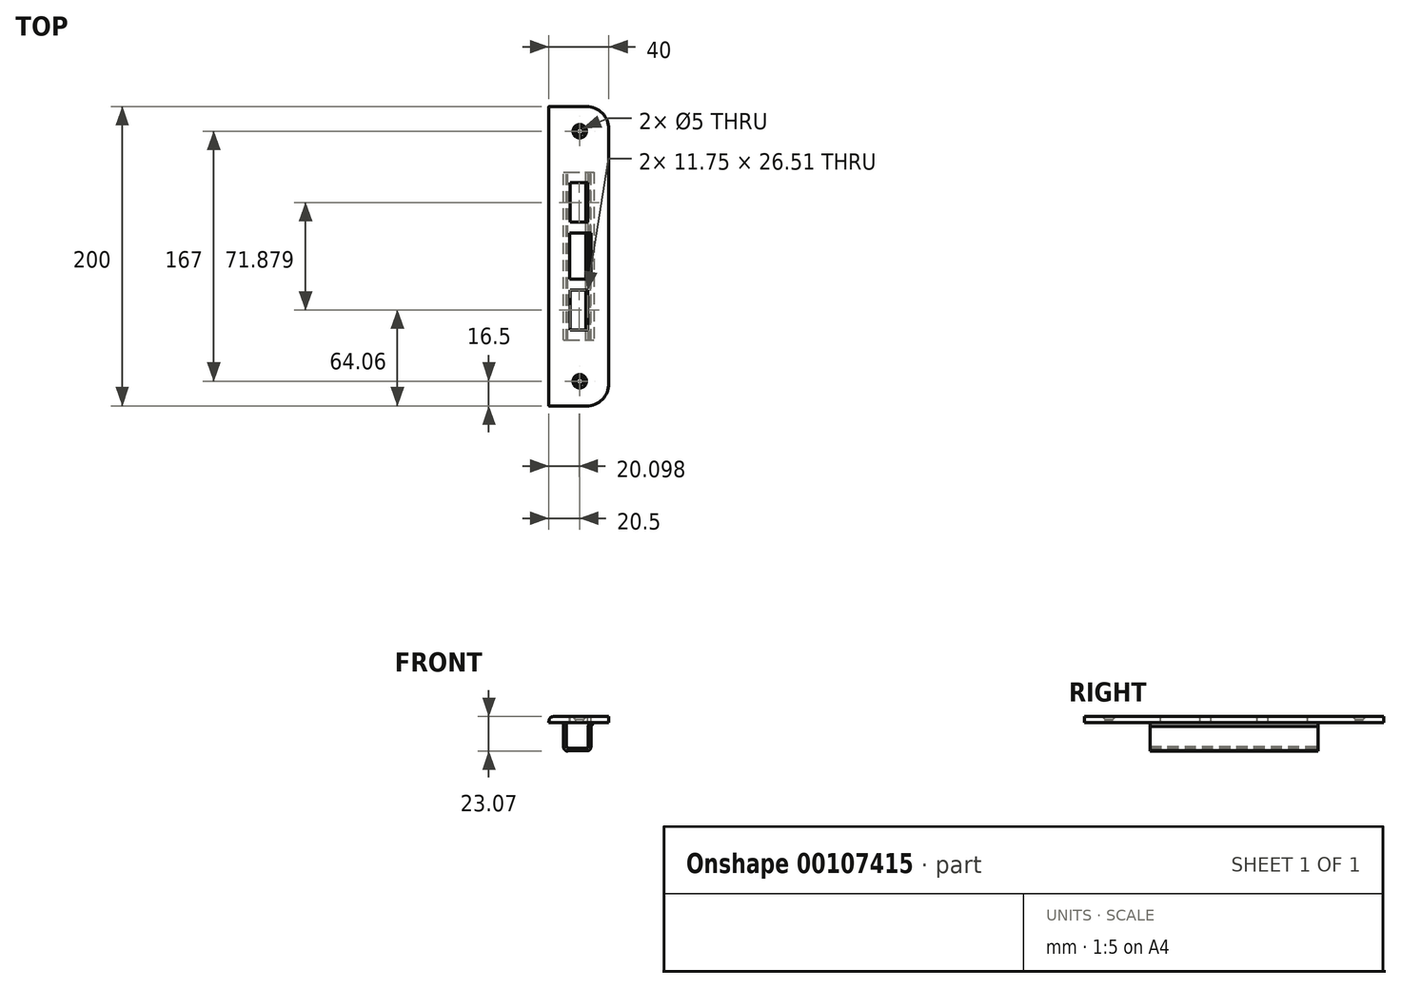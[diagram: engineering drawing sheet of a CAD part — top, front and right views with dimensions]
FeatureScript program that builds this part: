
annotation { "Feature Type Name" : "Feature", "Feature Type Description" : "" }
export const myFeature = defineFeature(function(context is Context, id is Id, definition is map)
    precondition{}
    {
        {
            var Q0;
            Q0=qCreatedBy(makeId("Top.planeOp"),FACE);
            var sketch = newSketch(context, id + "F0", { "sketchPlane" : qUnion([Q0])});
            skLineSegment(sketch, "E0", {"start": v(5, 100) * mm, "end": v(-20, 100) * mm});
            skLineSegment(sketch, "E1", {"start": v(-20, 100) * mm, "end": v(-20, -100) * mm});
            skLineSegment(sketch, "E2", {"start": v(-20, -100) * mm, "end": v(5, -100) * mm});
            skLineSegment(sketch, "E3", {"start": v(20, -85) * mm, "end": v(20, 85) * mm});
            skArc(sketch, "E4", {"start": v(20, 85) * mm, "mid": v(15.6, 95.6) * mm, "end": v(5, 100) * mm});
            skArc(sketch, "E5", {"start": v(5, -100) * mm, "mid": v(15.6, -95.6) * mm, "end": v(20, -85) * mm});
            skLineSegment(sketch, "E6.bottom", {"start": v(-5.77, 49.2) * mm, "end": v(5.97, 49.2) * mm});
            skLineSegment(sketch, "E6.top", {"start": v(-5.77, 22.69) * mm, "end": v(5.97, 22.69) * mm});
            skLineSegment(sketch, "E6.left", {"start": v(-5.77, 49.2) * mm, "end": v(-5.77, 22.69) * mm});
            skLineSegment(sketch, "E6.right", {"start": v(5.97, 49.2) * mm, "end": v(5.97, 22.69) * mm});
            skLineSegment(sketch, "E7.bottom", {"start": v(-5.77, -22.69) * mm, "end": v(5.97, -22.69) * mm});
            skLineSegment(sketch, "E7.top", {"start": v(-5.77, -49.2) * mm, "end": v(5.97, -49.2) * mm});
            skLineSegment(sketch, "E7.left", {"start": v(-5.77, -22.69) * mm, "end": v(-5.77, -49.2) * mm});
            skLineSegment(sketch, "E7.right", {"start": v(5.97, -22.69) * mm, "end": v(5.97, -49.2) * mm});
            skLineSegment(sketch, "E8.bottom", {"start": v(-6.34, 15.37) * mm, "end": v(8.23, 15.37) * mm});
            skLineSegment(sketch, "E8.top", {"start": v(-6.34, -15.37) * mm, "end": v(8.23, -15.37) * mm});
            skLineSegment(sketch, "E8.left", {"start": v(-6.34, 15.37) * mm, "end": v(-6.34, -15.37) * mm});
            skLineSegment(sketch, "E8.right", {"start": v(8.23, 15.37) * mm, "end": v(8.23, -15.37) * mm});
            skCircle(sketch, "E9", {"center": v(0.5, 83.5) * mm, "radius": 2.5 * mm});
            skCircle(sketch, "E10", {"center": v(0.5, -83.5) * mm, "radius": 2.5 * mm});
            skSolve(sketch);
        }
        {
            var Q0;
            Q0=makeQuery(id+"F0.imprint","IMPRINT",FACE,{"disambiguationData":[TD([[makeQuery(id+"F0.imprint","IMPRINT",EDGE,{"derivedFrom":sQuery(id+"F0.wireOp",EDGE,"E0")}),1.0]])]});
            extrude(context, id + "F1", {"entities" : qUnion([Q0]), "oppositeDirection" : true, "depth" : 4 * mm});
        }
        {
            var Q0;
            Q0=makeQuery(id+"F1.opExtrude","CAP_EDGE",EDGE,{"disambiguationData":[OSD([sQuery(id+"F0.wireOp",EDGE,"E10")])],"isStart":true});
            var Q1;
            Q1=makeQuery(id+"F1.opExtrude","CAP_EDGE",EDGE,{"disambiguationData":[OSD([sQuery(id+"F0.wireOp",EDGE,"E9")])],"isStart":true});
            chamfer(context, id + "F2", {"entities" : qUnion([Q0, Q1]), "width" : 2 * mm, "tangentPropagation" : true});
        }
        {
            var Q0;
            Q0=qCreatedBy(makeId("Front.planeOp"),FACE);
            var sketch = newSketch(context, id + "F3", { "sketchPlane" : qUnion([Q0])});
            skLineSegment(sketch, "E11.0", {"start": v(8.01, -6.65) * mm, "end": v(10.02, -3.9) * mm});
            skLineSegment(sketch, "E11.2", {"start": v(-10.24, -4) * mm, "end": v(-10.24, -20.07) * mm});
            skArc(sketch, "E11.3", {"start": v(-10.24, -20.07) * mm, "mid": v(-9.54, -22.15) * mm, "end": v(-7.56, -23.07) * mm});
            skLineSegment(sketch, "E11.4", {"start": v(-7.56, -23.07) * mm, "end": v(6.5, -22.78) * mm});
            skArc(sketch, "E11.5", {"start": v(6.5, -22.78) * mm, "mid": v(7.6, -21.73) * mm, "end": v(8, -20.26) * mm});
            skLineSegment(sketch, "E12.0", {"start": v(6.07, -6.17) * mm, "end": v(7.95, -3.39) * mm});
            skLineSegment(sketch, "E12.4", {"start": v(-7.11, -21) * mm, "end": v(4.72, -21) * mm});
            skArc(sketch, "E12.5", {"start": v(4.72, -21) * mm, "mid": v(5.77, -20.75) * mm, "end": v(6.25, -19.78) * mm});
            skLineSegment(sketch, "E13", {"start": v(-10.24, -4) * mm, "end": v(-8.37, -4) * mm});
            skLineSegment(sketch, "E14", {"start": v(7.95, -3.39) * mm, "end": v(10.02, -3.9) * mm});
            skLineSegment(sketch, "E15", {"start": v(-8.37, -4) * mm, "end": v(-8.37, -20.14) * mm});
            skArc(sketch, "E16", {"start": v(-8.37, -20.14) * mm, "mid": v(-7.88, -20.76) * mm, "end": v(-7.11, -21) * mm});
            skLineSegment(sketch, "E17", {"start": v(6.07, -6.17) * mm, "end": v(6.25, -19.78) * mm});
            skLineSegment(sketch, "E18", {"start": v(8.01, -6.65) * mm, "end": v(8, -20.26) * mm});
            skSolve(sketch);
        }
        {
            var Q0;
            Q0=makeQuery(id+"F3.imprint","IMPRINT",FACE,{"disambiguationData":[TD([[makeQuery(id+"F3.imprint","IMPRINT",EDGE,{"derivedFrom":sQuery(id+"F3.wireOp",EDGE,"E11.0")}),1.0]])]});
            extrude(context, id + "F4", {"entities" : qUnion([Q0]), "operationType" : NewBodyOperationType.ADD, "endBound" : BoundingType.SYMMETRIC, "depth" : 112 * mm});
        }
        {
            var Q0;
            Q0=makeQuery(id+"F1.opExtrude","CAP_EDGE",EDGE,{"disambiguationData":[OSD([sQuery(id+"F0.wireOp",EDGE,"E1")])],"isStart":true});
            fillet(context, id + "F5", {"entities" : qUnion([Q0]), "radius" : 3 * mm, "tangentPropagation" : true, "allowEdgeOverflow" : false});
        }
    });
